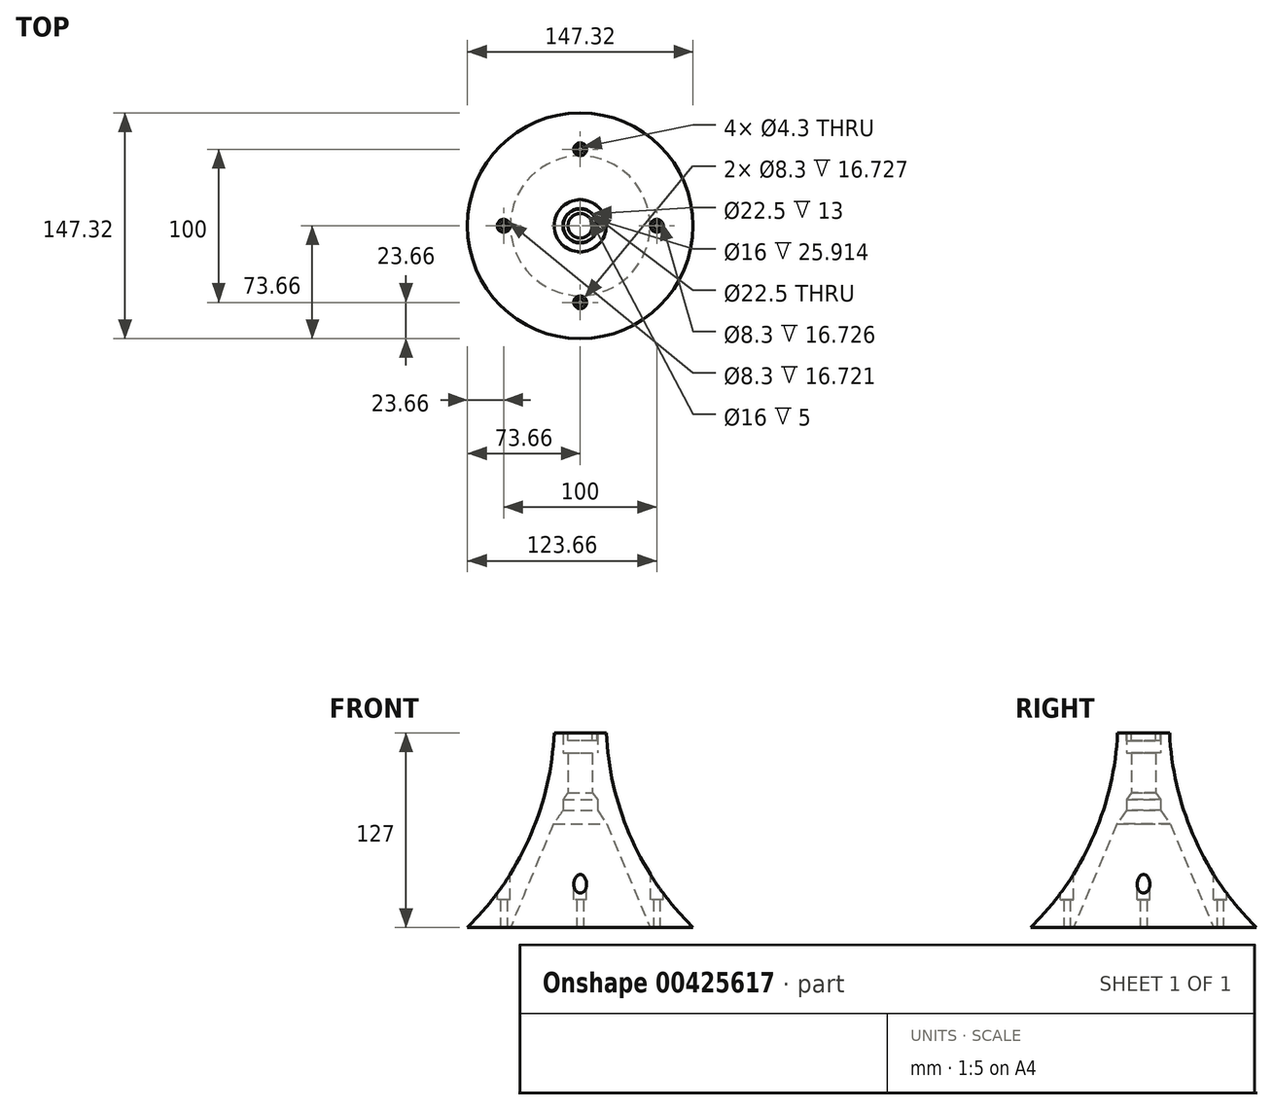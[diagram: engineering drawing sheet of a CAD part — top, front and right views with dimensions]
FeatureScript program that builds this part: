
annotation { "Feature Type Name" : "Feature", "Feature Type Description" : "" }
export const myFeature = defineFeature(function(context is Context, id is Id, definition is map)
    precondition{}
    {
        {
            var Q0;
            Q0=qCreatedBy(makeId("Front.planeOp"),FACE);
            var sketch = newSketch(context, id + "F0", { "sketchPlane" : qUnion([Q0])});
            skLineSegment(sketch, "E0", {"start": v(11.25, 127) * mm, "end": v(17, 127) * mm});
            skLineSegment(sketch, "E1", {"start": v(45.58, 0) * mm, "end": v(73.66, 0) * mm});
            skPoint(sketch, "E2", {"position": v(11.25, 127) * mm});
            skLineSegment(sketch, "E3.top", {"start": v(11.25, 114) * mm, "end": v(8, 114) * mm});
            skLineSegment(sketch, "E3.left", {"start": v(11.25, 127) * mm, "end": v(11.25, 114) * mm});
            skPoint(sketch, "E4.orphan", {"position": v(0, 127) * mm});
            skLineSegment(sketch, "E5", {"start": v(0, 0) * mm, "end": v(0, 127) * mm, "construction": true});
            skLineSegment(sketch, "E6", {"start": v(8, 88.09) * mm, "end": v(8, 114) * mm});
            skLineSegment(sketch, "E7", {"start": v(11.25, 83.44) * mm, "end": v(11.25, 76.44) * mm});
            skArc(sketch, "E8", {"start": v(17, 127) * mm, "mid": v(33.37, 58.16) * mm, "end": v(73.66, 0) * mm});
            skLineSegment(sketch, "E9", {"start": v(11.25, 76.44) * mm, "end": v(17.5, 67.52) * mm});
            skLineSegment(sketch, "E10", {"start": v(8, 88.09) * mm, "end": v(11.25, 83.44) * mm});
            skLineSegment(sketch, "E11", {"start": v(17.5, 67.52) * mm, "end": v(45.58, 0) * mm});
            skPoint(sketch, "E12.orphan", {"position": v(17.5, 0) * mm});
            skSolve(sketch);
        }
        {
            var Q0;
            Q0=makeQuery(id+"F0.imprint","IMPRINT",FACE,{"disambiguationData":[TD([[makeQuery(id+"F0.imprint","IMPRINT",EDGE,{"derivedFrom":sQuery(id+"F0.wireOp",EDGE,"E0")}),-1.0]])]});
            var Q1;
            Q1=sQuery(id+"F0.wireOp",EDGE,"E5");
            revolve(context, id + "F1", {"entities" : qUnion([Q0]), "axis" : qUnion([Q1]), "revolveType" : RevolveType.FULL});
        }
        {
            var Q0;
            Q0=makeQuery(id+"F1.opRevolve","SWEPT_FACE",FACE,{"disambiguationData":[OSD([sQuery(id+"F0.wireOp",EDGE,"E1")])]});
            var sketch = newSketch(context, id + "F2", { "sketchPlane" : qUnion([Q0])});
            skCircle(sketch, "E13", {"center": v(0, 0) * mm, "radius": 50 * mm, "construction": true});
            skPoint(sketch, "E14", {"position": v(50, 0) * mm});
            skPoint(sketch, "E15", {"position": v(0, 50) * mm});
            skPoint(sketch, "E16", {"position": v(-50, 0) * mm});
            skPoint(sketch, "E17", {"position": v(0, -50) * mm});
            skCircle(sketch, "E18", {"center": v(50, 0) * mm, "radius": 2.15 * mm});
            skCircle(sketch, "E19", {"center": v(0, 50) * mm, "radius": 2.15 * mm});
            skCircle(sketch, "E20", {"center": v(-50, 0) * mm, "radius": 2.15 * mm});
            skCircle(sketch, "E21", {"center": v(0, -50) * mm, "radius": 2.15 * mm});
            skSolve(sketch);
        }
        {
            var Q0;
            Q0 = qSketchRegion(id + "F2", true);
            extrude(context, id + "F3", {"entities" : qUnion([Q0]), "operationType" : NewBodyOperationType.REMOVE, "oppositeDirection" : true, "depth" : 10 * mm, "offsetDistance" : 25 * mm});
        }
        {
            var Q0;
            Q0=makeQuery(id+"F1.opRevolve","SWEPT_FACE",FACE,{"disambiguationData":[OSD([sQuery(id+"F0.wireOp",EDGE,"E1")])]});
            var sketch = newSketch(context, id + "F4", { "sketchPlane" : qUnion([Q0])});
            skCircle(sketch, "E22", {"center": v(0, 0) * mm, "radius": 50 * mm, "construction": true});
            skPoint(sketch, "E23", {"position": v(0, 50) * mm});
            skPoint(sketch, "E24", {"position": v(50, 0) * mm});
            skPoint(sketch, "E25", {"position": v(0, -50) * mm});
            skPoint(sketch, "E26", {"position": v(-50, 0) * mm});
            skCircle(sketch, "E27", {"center": v(0, 50) * mm, "radius": 2.15 * mm});
            skCircle(sketch, "E28", {"center": v(50, 0) * mm, "radius": 2.15 * mm});
            skCircle(sketch, "E29", {"center": v(-50, 0) * mm, "radius": 2.15 * mm});
            skCircle(sketch, "E30", {"center": v(0, -50) * mm, "radius": 2.15 * mm});
            skSolve(sketch);
        }
        {
            var Q0;
            Q0 = qSketchRegion(id + "F4", true);
            extrude(context, id + "F5", {"entities" : qUnion([Q0]), "operationType" : NewBodyOperationType.REMOVE, "endBound" : BoundingType.THROUGH_ALL, "oppositeDirection" : true, "depth" : 25 * mm, "offsetDistance" : 25 * mm});
        }
        {
            var Q0;
            Q0=qCreatedBy(makeId("Top.planeOp"),FACE);
            cPlane(context, id + "F6", {"entities" : qUnion([Q0]), "cplaneType" : CPlaneType.OFFSET, "offset" : 37 * mm, "width" : 150 * mm, "height" : 150 * mm});
        }
        {
            var Q0;
            Q0=qCreatedBy(id+"F6.planeOp",FACE);
            var sketch = newSketch(context, id + "F7", { "sketchPlane" : qUnion([Q0])});
            skCircle(sketch, "E31", {"center": v(0, 0) * mm, "radius": 50 * mm, "construction": true});
            skCircle(sketch, "E32", {"center": v(0, 50) * mm, "radius": 4.15 * mm});
            skCircle(sketch, "E33", {"center": v(50, 0) * mm, "radius": 4.15 * mm});
            skCircle(sketch, "E34", {"center": v(0, -50) * mm, "radius": 4.15 * mm});
            skCircle(sketch, "E35", {"center": v(-50, 0) * mm, "radius": 4.15 * mm});
            skSolve(sketch);
        }
        {
            var Q0;
            Q0 = qSketchRegion(id + "F7", true);
            extrude(context, id + "F8", {"entities" : qUnion([Q0]), "operationType" : NewBodyOperationType.REMOVE, "oppositeDirection" : true, "depth" : 19 * mm, "offsetDistance" : 25 * mm});
        }
        {
            var Q0;
            Q0=makeQuery(id+"F1.opRevolve","SWEPT_FACE",FACE,{"disambiguationData":[OSD([sQuery(id+"F0.wireOp",EDGE,"E0")])]});
            var sketch = newSketch(context, id + "F9", { "sketchPlane" : qUnion([Q0])});
            skCircle(sketch, "E36", {"center": v(0, 0) * mm, "radius": 11 * mm});
            skCircle(sketch, "E37", {"center": v(0, 0) * mm, "radius": 8 * mm});
            skPoint(sketch, "E38", {"position": v(11.25, 0) * mm});
            skSolve(sketch);
        }
        {
            var Q0;
            Q0 = qSketchRegion(id + "F9", true);
            extrude(context, id + "F10", {"entities" : qUnion([Q0]), "oppositeDirection" : true, "depth" : 5 * mm, "offsetDistance" : 25 * mm});
        }
    });
